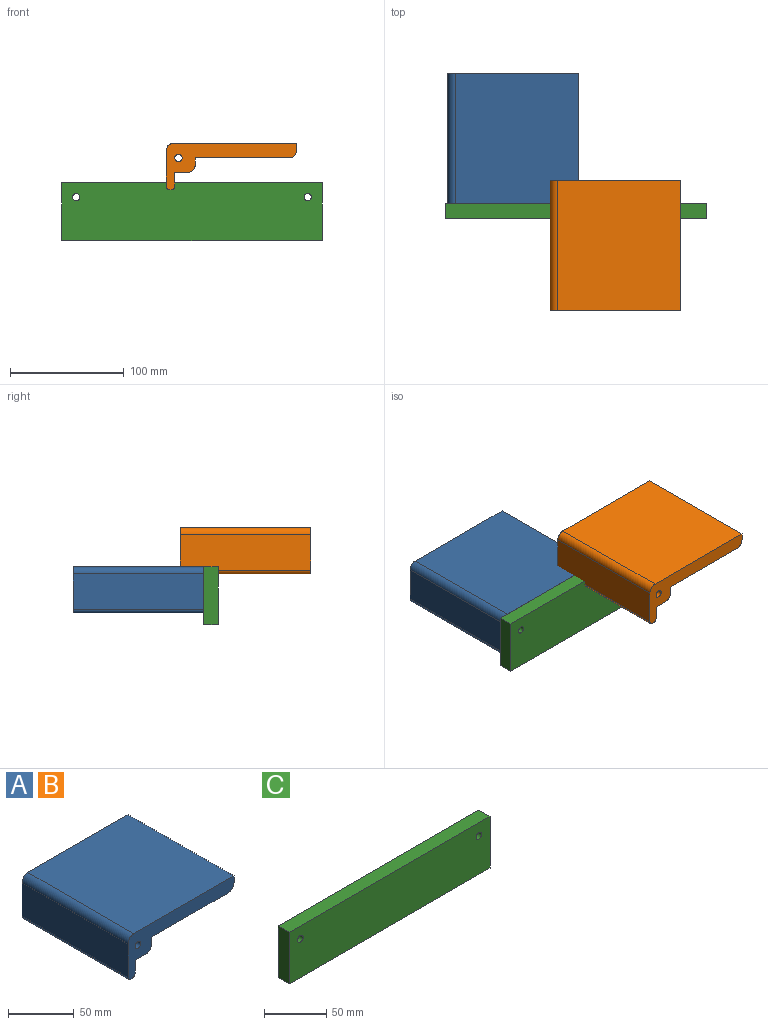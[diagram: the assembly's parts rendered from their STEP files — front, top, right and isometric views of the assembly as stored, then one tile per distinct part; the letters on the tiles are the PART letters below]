
ASSEMBLY  parts=3 mates=1
PART A: 16 faces, bbox 114.3x114.3x40.6 mm
  f0: cylinder r=3.17mm len=114.3mm, axis (0,1,0), area 570mm2, adj f1,f13,f14,f15
  f1: plane 114.3x1.27mm, normal (0,0,-1), area 145.2mm2, adj f0,f2,f14,f15
  f2: cylinder r=3.17mm len=114.3mm, axis (0,1,0), area 570mm2, adj f1,f3,f14,f15
  f3: plane 114.3x12.07mm, normal (1,0,0), area 1379mm2, adj f2,f4,f14,f15
  f4: plane 114.3x11.43mm, normal (0,0,-1), area 1306.4mm2, adj f3,f5,f14,f15
  f5: cylinder r=6.35mm len=114.3mm, axis (0,1,0), area 1140.1mm2, adj f4,f6,f14,f15
  f6: plane 114.3x6.35mm, normal (1,0,0), area 725.8mm2, adj f5,f7,f14,f15
  f7: plane 114.3x82.55mm, normal (0,0,-1), area 9435.5mm2, adj f6,f8,f14,f15
  f8: cylinder r=6.35mm len=114.3mm, axis (0,1,0), area 1140.1mm2, adj f7,f9,f14,f15
  f9: plane 114.3x6.35mm, normal (1,0,0), area 725.8mm2, adj f8,f10,f14,f15
  f10: plane 114.3x107.95mm, normal (0,0,1), area 12338.7mm2, adj f9,f11,f14,f15
  f11: cylinder r=6.35mm len=114.3mm, axis (0,1,0), area 1140.1mm2, adj f10,f13,f14,f15
  f12: cylinder r=3.17mm len=114.3mm, axis (0,1,0), area 2280.2mm2, adj f14,f15
  f13: plane 114.3x31.12mm, normal (-1,0,0), area 3556.4mm2, adj f0,f11,f14,f15
  f14: plane 114.3x40.64mm, normal (0,-1,0), area 1828.4mm2, adj f0,f1,f2,f3,f4,f5,f6,f7
  f15: plane 114.3x40.64mm, normal (0,1,0), area 1828.4mm2, adj f0,f1,f2,f3,f4,f5,f6,f7
PART B: same geometry as A
PART C: 8 faces, bbox 228.6x12.7x50.8 mm
  f0: plane 228.6x12.7mm, normal (0,0,1), area 2903.2mm2, adj f1,f5,f6,f7
  f1: plane 50.8x12.7mm, normal (-1,0,0), area 645.2mm2, adj f0,f2,f6,f7
  f2: plane 228.6x12.7mm, normal (0,0,-1), area 2903.2mm2, adj f1,f5,f6,f7
  f3: cylinder r=3.17mm len=12.7mm, axis (0,1,0), area 253.4mm2, adj f6,f7
  f4: cylinder r=3.17mm len=12.7mm, axis (0,1,0), area 253.4mm2, adj f6,f7
  f5: plane 50.8x12.7mm, normal (1,0,0), area 645.2mm2, adj f0,f2,f6,f7
  f6: plane 228.6x50.8mm, normal (0,-1,0), area 11549.5mm2, adj f0,f1,f2,f3,f4,f5
  f7: plane 228.6x50.8mm, normal (0,1,0), area 11549.5mm2, adj f0,f1,f2,f3,f4,f5
PLACE A t=(-3.85,114.3,0)mm
PLACE B t=(85.88,20.59,34.44)mm
PLACE C at identity
MATE pin_slot A.f12 <-> C.f4  axis (0,-1,0) through (12.7,0,-12.7)mm
